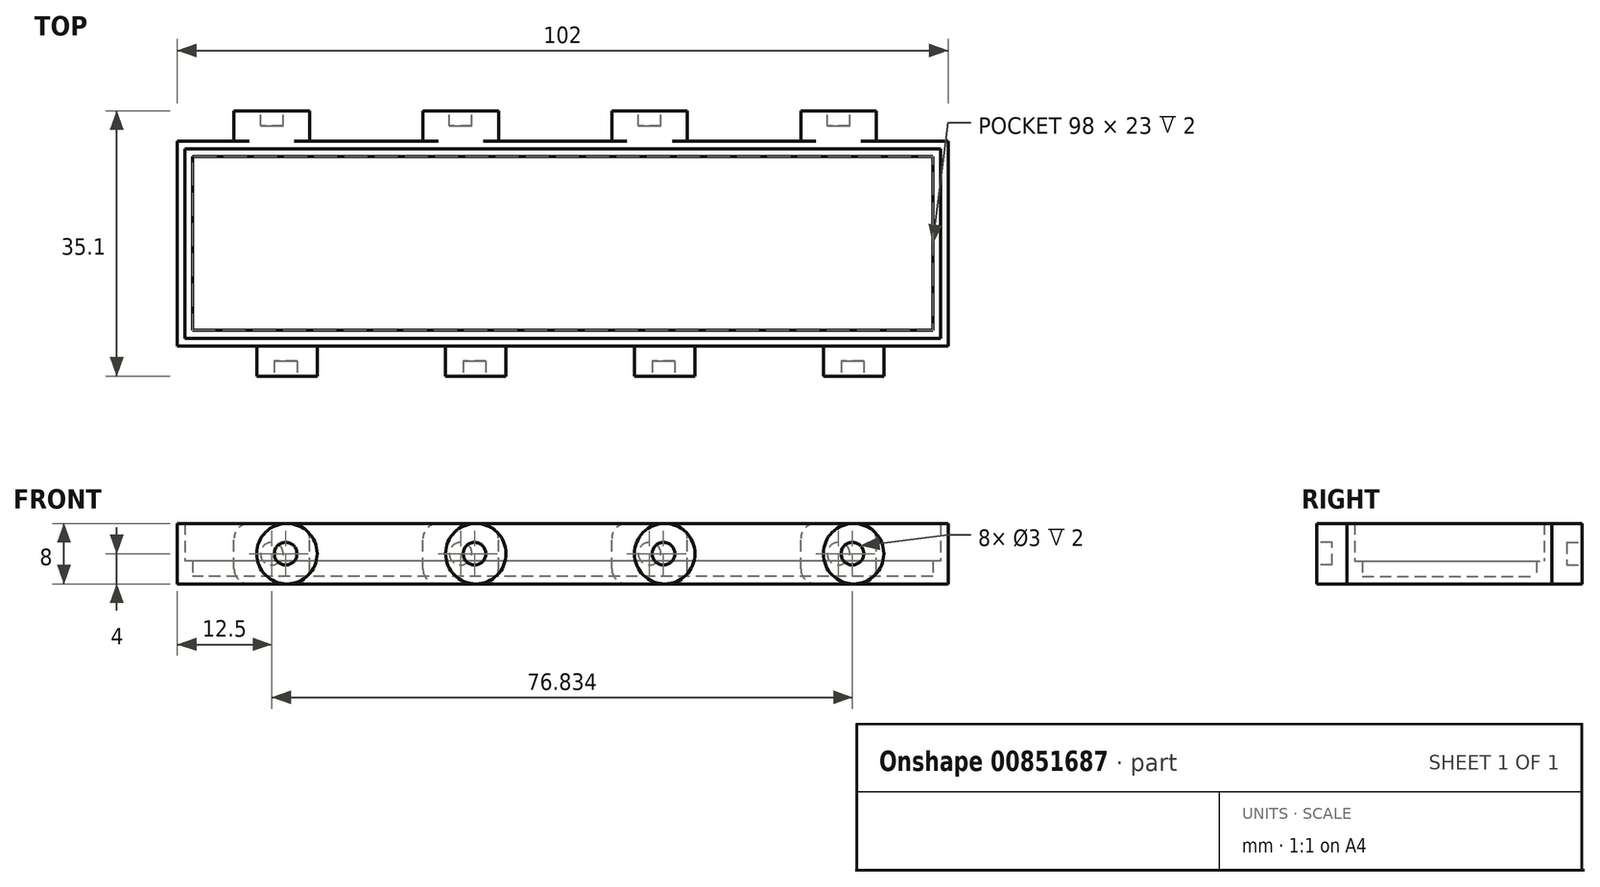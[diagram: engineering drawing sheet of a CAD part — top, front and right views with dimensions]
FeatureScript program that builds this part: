
annotation { "Feature Type Name" : "Feature", "Feature Type Description" : "" }
export const myFeature = defineFeature(function(context is Context, id is Id, definition is map)
    precondition{}
    {
        {
            var Q0;
            Q0=qCreatedBy(makeId("Top.planeOp"),FACE);
            var sketch = newSketch(context, id + "F0", { "sketchPlane" : qUnion([Q0])});
            skLineSegment(sketch, "E0.bottom", {"start": v(50, -12.55) * mm, "end": v(-50, -12.55) * mm});
            skLineSegment(sketch, "E0.top", {"start": v(50, 12.55) * mm, "end": v(-50, 12.55) * mm});
            skLineSegment(sketch, "E0.left", {"start": v(50, -12.55) * mm, "end": v(50, 12.55) * mm});
            skLineSegment(sketch, "E0.right", {"start": v(-50, -12.55) * mm, "end": v(-50, 12.55) * mm});
            skPoint(sketch, "E0.middle", {"position": v(0, 0) * mm});
            skLineSegment(sketch, "E1.bottom", {"start": v(51, -13.55) * mm, "end": v(-51, -13.55) * mm});
            skLineSegment(sketch, "E1.top", {"start": v(51, 13.55) * mm, "end": v(-51, 13.55) * mm});
            skLineSegment(sketch, "E1.left", {"start": v(51, -13.55) * mm, "end": v(51, 13.55) * mm});
            skLineSegment(sketch, "E1.right", {"start": v(-51, -13.55) * mm, "end": v(-51, 13.55) * mm});
            skSolve(sketch);
        }
        {
            var Q0;
            Q0=makeQuery(id+"F0.imprint","IMPRINT",FACE,{"disambiguationData":[TD([[makeQuery(id+"F0.imprint","IMPRINT",EDGE,{"derivedFrom":sQuery(id+"F0.wireOp",EDGE,"E0.bottom")}),1.0]])]});
            extrude(context, id + "F1", {"entities" : qUnion([Q0]), "depth" : 8 * mm, "offsetDistance" : 25 * mm});
        }
        {
            var Q0;
            Q0=makeQuery(id+"F0.imprint","IMPRINT",FACE,{"disambiguationData":[TD([[makeQuery(id+"F0.imprint","IMPRINT",EDGE,{"derivedFrom":sQuery(id+"F0.wireOp",EDGE,"E0.bottom")}),-1.0]])]});
            extrude(context, id + "F2", {"entities" : qUnion([Q0]), "operationType" : NewBodyOperationType.ADD, "depth" : 1 * mm, "offsetDistance" : 25 * mm});
        }
        {
            var Q0;
            Q0=makeQuery(id+"F2.opExtrude","CAP_FACE",FACE,{"disambiguationData":[OSD([sQuery(id+"F0.wireOp",EDGE,"E0.bottom"),sQuery(id+"F0.wireOp",EDGE,"E0.top"),sQuery(id+"F0.wireOp",EDGE,"E0.left"),sQuery(id+"F0.wireOp",EDGE,"E0.right")])],"isStart":false});
            var sketch = newSketch(context, id + "F3", { "sketchPlane" : qUnion([Q0])});
            skLineSegment(sketch, "E2.bottom", {"start": v(49, -11.5) * mm, "end": v(-49, -11.5) * mm});
            skLineSegment(sketch, "E2.top", {"start": v(49, 11.5) * mm, "end": v(-49, 11.5) * mm});
            skLineSegment(sketch, "E2.left", {"start": v(49, -11.5) * mm, "end": v(49, 11.5) * mm});
            skLineSegment(sketch, "E2.right", {"start": v(-49, -11.5) * mm, "end": v(-49, 11.5) * mm});
            skPoint(sketch, "E2.middle", {"position": v(0, 0) * mm});
            skSolve(sketch);
        }
        {
            var Q0;
            Q0=makeQuery(id+"F3.imprint","IMPRINT",FACE,{"disambiguationData":[TD([[makeQuery(id+"F3.imprint","IMPRINT",EDGE,{"derivedFrom":sQuery(id+"F3.wireOp",EDGE,"E2.bottom")}),1.0]])]});
            extrude(context, id + "F4", {"entities" : qUnion([Q0]), "operationType" : NewBodyOperationType.ADD, "depth" : 2 * mm, "offsetDistance" : 25 * mm});
        }
        {
            var Q0;
            Q0=makeQuery(id+"F1.opExtrude","SWEPT_FACE",FACE,{"disambiguationData":[OSD([sQuery(id+"F0.wireOp",EDGE,"E1.bottom")])]});
            var sketch = newSketch(context, id + "F5", { "sketchPlane" : qUnion([Q0])});
            skLineSegment(sketch, "E3", {"start": v(-51, 4) * mm, "end": v(-36.5, 4) * mm, "construction": true});
            skLineSegment(sketch, "E4", {"start": v(-36.5, 4) * mm, "end": v(-11.5, 4) * mm, "construction": true});
            skLineSegment(sketch, "E5", {"start": v(-11.5, 4) * mm, "end": v(13.5, 4) * mm, "construction": true});
            skLineSegment(sketch, "E6", {"start": v(13.5, 4) * mm, "end": v(38.5, 4) * mm, "construction": true});
            skLineSegment(sketch, "E7", {"start": v(38.5, 4) * mm, "end": v(51, 4) * mm, "construction": true});
            skCircle(sketch, "E8", {"center": v(-36.5, 4) * mm, "radius": 4 * mm});
            skCircle(sketch, "E9.1.0.0", {"center": v(-11.5, 4) * mm, "radius": 4 * mm});
            skCircle(sketch, "E9.2.0.0", {"center": v(13.5, 4) * mm, "radius": 4 * mm});
            skCircle(sketch, "E9.3.0.0", {"center": v(38.5, 4) * mm, "radius": 4 * mm});
            skSolve(sketch);
        }
        {
            var Q0;
            Q0=makeQuery(id+"F5.imprint","IMPRINT",FACE,{"disambiguationData":[TD([[makeQuery(id+"F5.imprint","IMPRINT",EDGE,{"derivedFrom":sQuery(id+"F5.wireOp",EDGE,"21R3qTEr-d9QE-zeYS-lOOO-46okw6DRriXY")}),1.0]])]});
            var Q1;
            {var subQ0=sQuery(id+"F5.wireOp",EDGE,"E8");var subQ1=sQuery(id+"F0.wireOp",EDGE,"E1.bottom");var subQ2=makeQuery(id+"F5.imprint","INTERSECT",VERTEX,{"derivedFrom":[makeQuery(id+"F1.opExtrude","CAP_EDGE",EDGE,{"disambiguationData":[OSD([subQ1])],"isStart":true}),subQ0]});Q1=makeQuery(id+"F5.imprint","IMPRINT",FACE,{"disambiguationData":[TD([[makeQuery(id+"F5.imprint","IMPRINT",EDGE,{"disambiguationData":[TD([[subQ2,1.0]])],"derivedFrom":subQ0}),1.0]])]});}
            var Q2;
            {var subQ0=sQuery(id+"F5.wireOp",EDGE,"6V1pwvQt-yFFR-5VMJ-1m6w-qiaQHFsyWvq4");var subQ1=sQuery(id+"F0.wireOp",EDGE,"E1.bottom");var subQ2=makeQuery(id+"F5.imprint","INTERSECT",VERTEX,{"derivedFrom":[makeQuery(id+"F1.opExtrude","CAP_EDGE",EDGE,{"disambiguationData":[OSD([subQ1])],"isStart":true}),subQ0]});Q2=makeQuery(id+"F5.imprint","IMPRINT",FACE,{"disambiguationData":[TD([[makeQuery(id+"F5.imprint","IMPRINT",EDGE,{"disambiguationData":[TD([[subQ2,1.0]])],"derivedFrom":subQ0}),1.0]])]});}
            var Q3;
            {var subQ0=sQuery(id+"F5.wireOp",EDGE,"Y8gwPjQ0-TZgt-acKN-ooFg-tuIaiMLCC5Xz");var subQ1=sQuery(id+"F0.wireOp",EDGE,"E1.bottom");var subQ2=makeQuery(id+"F5.imprint","INTERSECT",VERTEX,{"derivedFrom":[makeQuery(id+"F1.opExtrude","CAP_EDGE",EDGE,{"disambiguationData":[OSD([subQ1])],"isStart":true}),subQ0]});Q3=makeQuery(id+"F5.imprint","IMPRINT",FACE,{"disambiguationData":[TD([[makeQuery(id+"F5.imprint","IMPRINT",EDGE,{"disambiguationData":[TD([[subQ2,1.0]])],"derivedFrom":subQ0}),1.0]])]});}
            var Q4;
            {var subQ0=sQuery(id+"F5.wireOp",EDGE,"E9.1.0.0");var subQ1=sQuery(id+"F0.wireOp",EDGE,"E1.bottom");var subQ2=makeQuery(id+"F5.imprint","INTERSECT",VERTEX,{"derivedFrom":[makeQuery(id+"F1.opExtrude","CAP_EDGE",EDGE,{"disambiguationData":[OSD([subQ1])],"isStart":true}),subQ0]});Q4=makeQuery(id+"F5.imprint","IMPRINT",FACE,{"disambiguationData":[TD([[makeQuery(id+"F5.imprint","IMPRINT",EDGE,{"disambiguationData":[TD([[subQ2,1.0]])],"derivedFrom":subQ0}),1.0]])]});}
            var Q5;
            {var subQ0=sQuery(id+"F5.wireOp",EDGE,"E9.2.0.0");var subQ1=sQuery(id+"F0.wireOp",EDGE,"E1.bottom");var subQ2=makeQuery(id+"F5.imprint","INTERSECT",VERTEX,{"derivedFrom":[makeQuery(id+"F1.opExtrude","CAP_EDGE",EDGE,{"disambiguationData":[OSD([subQ1])],"isStart":true}),subQ0]});Q5=makeQuery(id+"F5.imprint","IMPRINT",FACE,{"disambiguationData":[TD([[makeQuery(id+"F5.imprint","IMPRINT",EDGE,{"disambiguationData":[TD([[subQ2,1.0]])],"derivedFrom":subQ0}),1.0]])]});}
            var Q6;
            {var subQ0=sQuery(id+"F5.wireOp",EDGE,"E9.3.0.0");var subQ1=sQuery(id+"F0.wireOp",EDGE,"E1.bottom");var subQ2=makeQuery(id+"F5.imprint","INTERSECT",VERTEX,{"derivedFrom":[makeQuery(id+"F1.opExtrude","CAP_EDGE",EDGE,{"disambiguationData":[OSD([subQ1])],"isStart":true}),subQ0]});Q6=makeQuery(id+"F5.imprint","IMPRINT",FACE,{"disambiguationData":[TD([[makeQuery(id+"F5.imprint","IMPRINT",EDGE,{"disambiguationData":[TD([[subQ2,1.0]])],"derivedFrom":subQ0}),1.0]])]});}
            extrude(context, id + "F6", {"entities" : qUnion([Q0, Q1, Q2, Q3, Q4, Q5, Q6]), "operationType" : NewBodyOperationType.ADD, "depth" : 4 * mm, "offsetDistance" : 25 * mm});
        }
        {
            var Q0;
            Q0=makeQuery(id+"F6.opExtrude","CAP_FACE",FACE,{"disambiguationData":[OSD([sQuery(id+"F5.wireOp",EDGE,"E8")])],"isStart":false});
            var sketch = newSketch(context, id + "F7", { "sketchPlane" : qUnion([Q0])});
            skLineSegment(sketch, "E10", {"start": v(-36.67, 8) * mm, "end": v(-36.67, 0) * mm, "construction": true});
            skLineSegment(sketch, "E11", {"start": v(-36.67, 4) * mm, "end": v(-32.2, 4) * mm, "construction": true});
            skCircle(sketch, "E12", {"center": v(-36.67, 4) * mm, "radius": 1.5 * mm});
            skCircle(sketch, "E13.1.0.0", {"center": v(-11.67, 4) * mm, "radius": 1.5 * mm});
            skCircle(sketch, "E13.2.0.0", {"center": v(13.33, 4) * mm, "radius": 1.5 * mm});
            skCircle(sketch, "E13.3.0.0", {"center": v(38.33, 4) * mm, "radius": 1.5 * mm});
            skLineSegment(sketch, "E13.direction1", {"start": v(-36.67, 4) * mm, "end": v(-11.67, 4) * mm, "construction": true});
            skSolve(sketch);
        }
        {
            var Q0;
            Q0=makeQuery(id+"F7.imprint","IMPRINT",FACE,{"disambiguationData":[TD([[makeQuery(id+"F7.imprint","IMPRINT",EDGE,{"derivedFrom":sQuery(id+"F7.wireOp",EDGE,"E12")}),1.0]])]});
            var Q1;
            Q1=makeQuery(id+"F7.imprint","IMPRINT",FACE,{"disambiguationData":[TD([[makeQuery(id+"F7.imprint","IMPRINT",EDGE,{"derivedFrom":sQuery(id+"F7.wireOp",EDGE,"E13.1.0.0")}),1.0]])]});
            var Q2;
            Q2=makeQuery(id+"F7.imprint","IMPRINT",FACE,{"disambiguationData":[TD([[makeQuery(id+"F7.imprint","IMPRINT",EDGE,{"derivedFrom":sQuery(id+"F7.wireOp",EDGE,"E13.2.0.0")}),1.0]])]});
            var Q3;
            Q3=makeQuery(id+"F7.imprint","IMPRINT",FACE,{"disambiguationData":[TD([[makeQuery(id+"F7.imprint","IMPRINT",EDGE,{"derivedFrom":sQuery(id+"F7.wireOp",EDGE,"E13.3.0.0")}),1.0]])]});
            extrude(context, id + "F8", {"entities" : qUnion([Q0, Q1, Q2, Q3]), "operationType" : NewBodyOperationType.REMOVE, "oppositeDirection" : true, "depth" : 2 * mm, "offsetDistance" : 25 * mm});
        }
        {
            var Q0;
            Q0=makeQuery(id+"F1.opExtrude","SWEPT_FACE",FACE,{"disambiguationData":[OSD([sQuery(id+"F0.wireOp",EDGE,"E1.top")])]});
            var sketch = newSketch(context, id + "F9", { "sketchPlane" : qUnion([Q0])});
            skLineSegment(sketch, "E14", {"start": v(-51, 4) * mm, "end": v(-36.5, 4) * mm, "construction": true});
            skLineSegment(sketch, "E15", {"start": v(-36.5, 4) * mm, "end": v(-11.5, 4) * mm, "construction": true});
            skLineSegment(sketch, "E16", {"start": v(-11.5, 4) * mm, "end": v(13.5, 4) * mm, "construction": true});
            skLineSegment(sketch, "E17", {"start": v(13.5, 4) * mm, "end": v(38.5, 4) * mm, "construction": true});
            skLineSegment(sketch, "E18.bottom", {"start": v(-33.5, 0) * mm, "end": v(-39.5, 0) * mm});
            skLineSegment(sketch, "E18.top", {"start": v(-33.5, 8) * mm, "end": v(-39.5, 8) * mm});
            skLineSegment(sketch, "E18.left", {"start": v(-31.5, 2) * mm, "end": v(-31.5, 6) * mm});
            skLineSegment(sketch, "E18.right", {"start": v(-41.5, 2) * mm, "end": v(-41.5, 6) * mm});
            skPoint(sketch, "E18.middle", {"position": v(-36.5, 4) * mm});
            skPoint(sketch, "E19.visualSharp", {"position": v(-31.5, 8) * mm});
            skArc(sketch, "E19.filletArc", {"start": v(-31.5, 6) * mm, "mid": v(-32.09, 7.41) * mm, "end": v(-33.5, 8) * mm});
            skPoint(sketch, "E20.visualSharp", {"position": v(-31.5, 0) * mm});
            skArc(sketch, "E20.filletArc", {"start": v(-33.5, 0) * mm, "mid": v(-32.09, 0.59) * mm, "end": v(-31.5, 2) * mm});
            skPoint(sketch, "E21.visualSharp", {"position": v(-41.5, 0) * mm});
            skArc(sketch, "E21.filletArc", {"start": v(-41.5, 2) * mm, "mid": v(-40.91, 0.59) * mm, "end": v(-39.5, 0) * mm});
            skPoint(sketch, "E22.visualSharp", {"position": v(-41.5, 8) * mm});
            skArc(sketch, "E22.filletArc", {"start": v(-39.5, 8) * mm, "mid": v(-40.91, 7.41) * mm, "end": v(-41.5, 6) * mm});
            skLineSegment(sketch, "E23.1.0.0", {"start": v(-8.5, 8) * mm, "end": v(-14.5, 8) * mm});
            skArc(sketch, "E23.1.0.1", {"start": v(-6.5, 6) * mm, "mid": v(-7.09, 7.41) * mm, "end": v(-8.5, 8) * mm});
            skLineSegment(sketch, "E23.1.0.2", {"start": v(-6.5, 2) * mm, "end": v(-6.5, 6) * mm});
            skArc(sketch, "E23.1.0.3", {"start": v(-8.5, 0) * mm, "mid": v(-7.09, 0.59) * mm, "end": v(-6.5, 2) * mm});
            skLineSegment(sketch, "E23.1.0.4", {"start": v(-8.5, 0) * mm, "end": v(-14.5, 0) * mm});
            skArc(sketch, "E23.1.0.5", {"start": v(-16.5, 2) * mm, "mid": v(-15.91, 0.59) * mm, "end": v(-14.5, 0) * mm});
            skLineSegment(sketch, "E23.1.0.6", {"start": v(-16.5, 2) * mm, "end": v(-16.5, 6) * mm});
            skArc(sketch, "E23.1.0.7", {"start": v(-14.5, 8) * mm, "mid": v(-15.91, 7.41) * mm, "end": v(-16.5, 6) * mm});
            skLineSegment(sketch, "E23.2.0.0", {"start": v(16.5, 8) * mm, "end": v(10.5, 8) * mm});
            skArc(sketch, "E23.2.0.1", {"start": v(18.5, 6) * mm, "mid": v(17.91, 7.41) * mm, "end": v(16.5, 8) * mm});
            skLineSegment(sketch, "E23.2.0.2", {"start": v(18.5, 2) * mm, "end": v(18.5, 6) * mm});
            skArc(sketch, "E23.2.0.3", {"start": v(16.5, 0) * mm, "mid": v(17.91, 0.59) * mm, "end": v(18.5, 2) * mm});
            skLineSegment(sketch, "E23.2.0.4", {"start": v(16.5, 0) * mm, "end": v(10.5, 0) * mm});
            skArc(sketch, "E23.2.0.5", {"start": v(8.5, 2) * mm, "mid": v(9.09, 0.59) * mm, "end": v(10.5, 0) * mm});
            skLineSegment(sketch, "E23.2.0.6", {"start": v(8.5, 2) * mm, "end": v(8.5, 6) * mm});
            skArc(sketch, "E23.2.0.7", {"start": v(10.5, 8) * mm, "mid": v(9.09, 7.41) * mm, "end": v(8.5, 6) * mm});
            skLineSegment(sketch, "E23.3.0.0", {"start": v(41.5, 8) * mm, "end": v(35.5, 8) * mm});
            skArc(sketch, "E23.3.0.1", {"start": v(43.5, 6) * mm, "mid": v(42.91, 7.41) * mm, "end": v(41.5, 8) * mm});
            skLineSegment(sketch, "E23.3.0.2", {"start": v(43.5, 2) * mm, "end": v(43.5, 6) * mm});
            skArc(sketch, "E23.3.0.3", {"start": v(41.5, 0) * mm, "mid": v(42.91, 0.59) * mm, "end": v(43.5, 2) * mm});
            skLineSegment(sketch, "E23.3.0.4", {"start": v(41.5, 0) * mm, "end": v(35.5, 0) * mm});
            skArc(sketch, "E23.3.0.5", {"start": v(33.5, 2) * mm, "mid": v(34.09, 0.59) * mm, "end": v(35.5, 0) * mm});
            skLineSegment(sketch, "E23.3.0.6", {"start": v(33.5, 2) * mm, "end": v(33.5, 6) * mm});
            skArc(sketch, "E23.3.0.7", {"start": v(35.5, 8) * mm, "mid": v(34.09, 7.41) * mm, "end": v(33.5, 6) * mm});
            skLineSegment(sketch, "E23.direction1", {"start": v(-39.5, 8) * mm, "end": v(-14.5, 8) * mm, "construction": true});
            skSolve(sketch);
        }
        {
            var Q0;
            Q0=makeQuery(id+"F9.imprint","IMPRINT",FACE,{"disambiguationData":[TD([[makeQuery(id+"F9.imprint","IMPRINT",EDGE,{"derivedFrom":sQuery(id+"F9.wireOp",EDGE,"E18.bottom")}),1.0]])]});
            var Q1;
            Q1=makeQuery(id+"F9.imprint","IMPRINT",FACE,{"disambiguationData":[TD([[makeQuery(id+"F9.imprint","IMPRINT",EDGE,{"derivedFrom":sQuery(id+"F9.wireOp",EDGE,"E23.1.0.0")}),-1.0]])]});
            var Q2;
            Q2=makeQuery(id+"F9.imprint","IMPRINT",FACE,{"disambiguationData":[TD([[makeQuery(id+"F9.imprint","IMPRINT",EDGE,{"derivedFrom":sQuery(id+"F9.wireOp",EDGE,"E23.2.0.0")}),-1.0]])]});
            var Q3;
            Q3=makeQuery(id+"F9.imprint","IMPRINT",FACE,{"disambiguationData":[TD([[makeQuery(id+"F9.imprint","IMPRINT",EDGE,{"derivedFrom":sQuery(id+"F9.wireOp",EDGE,"E23.3.0.0")}),-1.0]])]});
            extrude(context, id + "F10", {"entities" : qUnion([Q0, Q1, Q2, Q3]), "operationType" : NewBodyOperationType.ADD, "depth" : 4 * mm, "offsetDistance" : 25 * mm});
        }
        {
            var Q0;
            Q0=makeQuery(id+"F10.opExtrude","CAP_FACE",FACE,{"disambiguationData":[OSD([sQuery(id+"F9.wireOp",EDGE,"E18.bottom"),sQuery(id+"F9.wireOp",EDGE,"E18.top"),sQuery(id+"F9.wireOp",EDGE,"E18.left"),sQuery(id+"F9.wireOp",EDGE,"E18.right"),sQuery(id+"F9.wireOp",EDGE,"E19.filletArc"),sQuery(id+"F9.wireOp",EDGE,"E20.filletArc"),sQuery(id+"F9.wireOp",EDGE,"E21.filletArc"),sQuery(id+"F9.wireOp",EDGE,"E22.filletArc")])],"isStart":false});
            var sketch = newSketch(context, id + "F11", { "sketchPlane" : qUnion([Q0])});
            skLineSegment(sketch, "E24", {"start": v(-36.5, 8) * mm, "end": v(-36.5, 0) * mm, "construction": true});
            skLineSegment(sketch, "E25", {"start": v(-36.5, 0) * mm, "end": v(-36.5, 4) * mm, "construction": true});
            skLineSegment(sketch, "E26", {"start": v(-36.5, 4) * mm, "end": v(-34.17, 4) * mm, "construction": true});
            skCircle(sketch, "E27", {"center": v(-36.5, 4) * mm, "radius": 1.5 * mm});
            skCircle(sketch, "E28.1.0.0", {"center": v(-11.5, 4) * mm, "radius": 1.5 * mm});
            skCircle(sketch, "E28.2.0.0", {"center": v(13.5, 4) * mm, "radius": 1.5 * mm});
            skCircle(sketch, "E28.3.0.0", {"center": v(38.5, 4) * mm, "radius": 1.5 * mm});
            skLineSegment(sketch, "E28.direction1", {"start": v(-36.5, 4) * mm, "end": v(-11.5, 4) * mm, "construction": true});
            skSolve(sketch);
        }
        {
            var Q0;
            Q0=makeQuery(id+"F11.imprint","IMPRINT",FACE,{"disambiguationData":[TD([[makeQuery(id+"F11.imprint","IMPRINT",EDGE,{"derivedFrom":sQuery(id+"F11.wireOp",EDGE,"E27")}),1.0]])]});
            var Q1;
            Q1=makeQuery(id+"F11.imprint","IMPRINT",FACE,{"disambiguationData":[TD([[makeQuery(id+"F11.imprint","IMPRINT",EDGE,{"derivedFrom":sQuery(id+"F11.wireOp",EDGE,"E28.1.0.0")}),1.0]])]});
            var Q2;
            Q2=makeQuery(id+"F11.imprint","IMPRINT",FACE,{"disambiguationData":[TD([[makeQuery(id+"F11.imprint","IMPRINT",EDGE,{"derivedFrom":sQuery(id+"F11.wireOp",EDGE,"E28.2.0.0")}),1.0]])]});
            var Q3;
            Q3=makeQuery(id+"F11.imprint","IMPRINT",FACE,{"disambiguationData":[TD([[makeQuery(id+"F11.imprint","IMPRINT",EDGE,{"derivedFrom":sQuery(id+"F11.wireOp",EDGE,"E28.3.0.0")}),1.0]])]});
            extrude(context, id + "F12", {"entities" : qUnion([Q0, Q1, Q2, Q3]), "operationType" : NewBodyOperationType.REMOVE, "oppositeDirection" : true, "depth" : 2 * mm, "offsetDistance" : 25 * mm});
        }
    });
